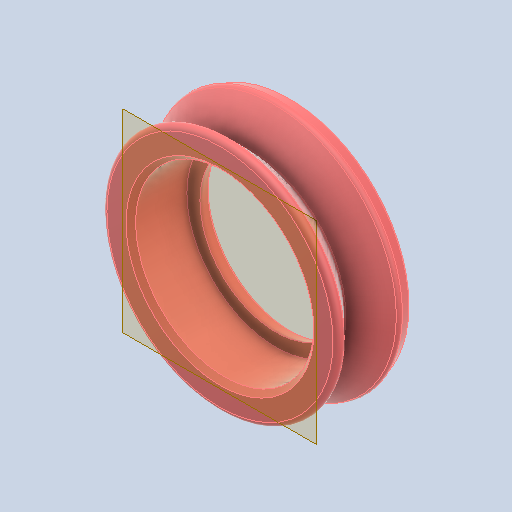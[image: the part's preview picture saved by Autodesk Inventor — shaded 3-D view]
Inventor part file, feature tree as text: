
AUTODESK INVENTOR PART (.ipt)
format: ipt  version: 2022 (Build 260153000, 153)  size: 220,160 bytes
history: native  units: in
note: dims shown in document units (in); Inventor stores cm internally (conversion verified against a paired STEP export)
features: other x3, sketch x1, plane x1
ambient origin geometry x8: Origin, YZ Plane, XZ Plane, XY Plane, X Axis, Y Axis, Z Axis, Center Point
bodies: Solid1 (feature_tree)
feature tree (5):
  other  "vroller_MIR.ipt"
  other  "Solid1::vroller_MIR.ipt"
  other  "TaggingFeature1"
  sketch  "Sketch1"  dims[d0=0.3937in]
  plane  "Work Plane1"
